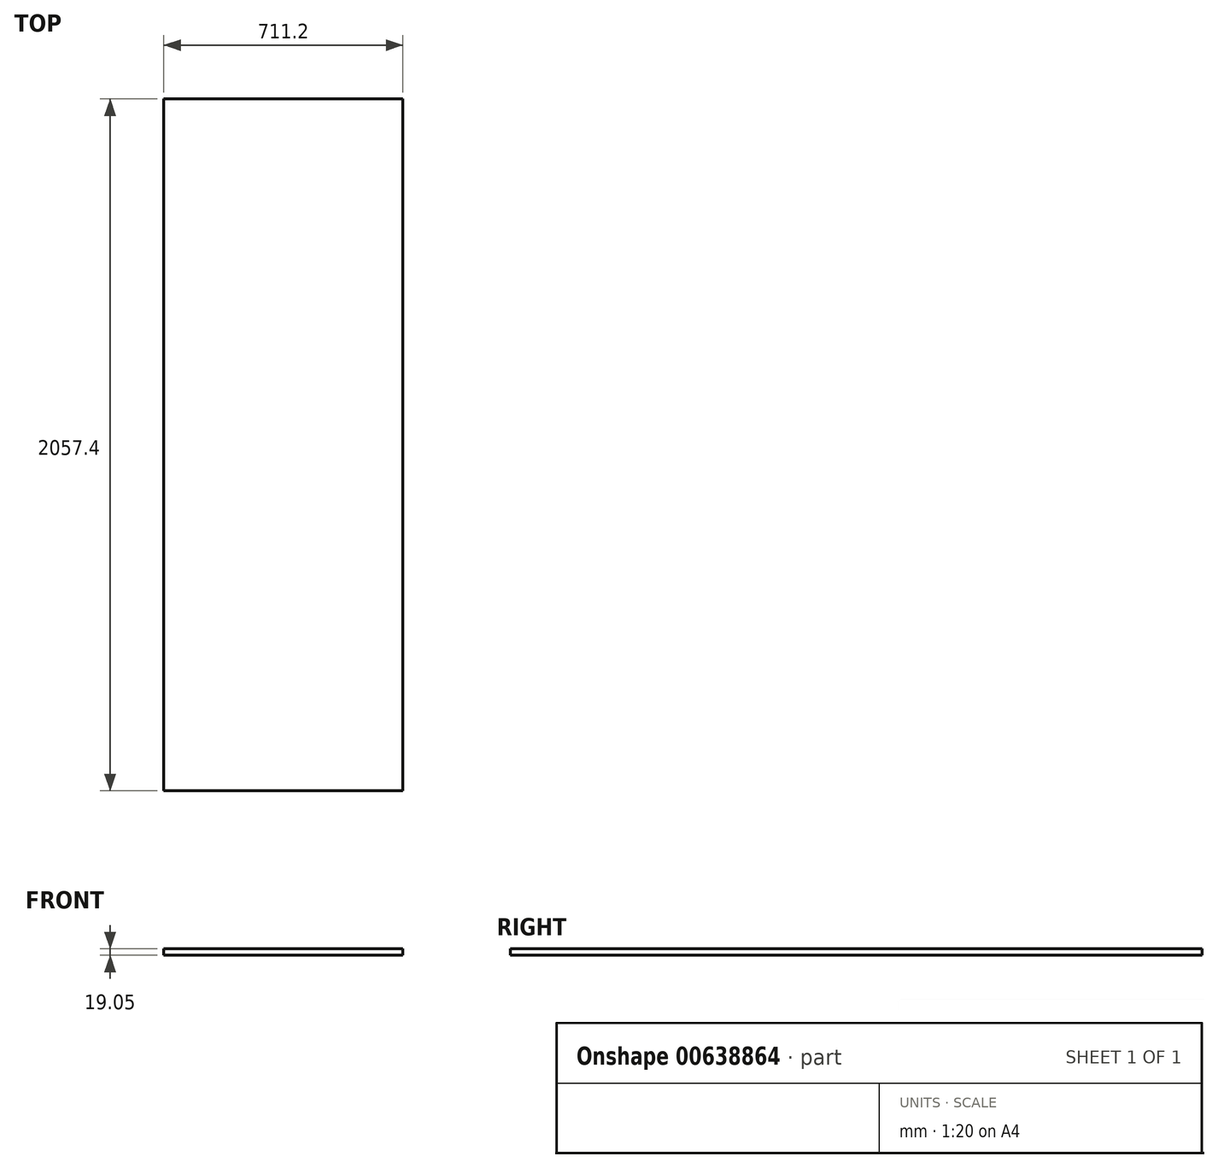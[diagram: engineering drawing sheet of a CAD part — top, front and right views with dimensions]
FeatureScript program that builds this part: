
annotation { "Feature Type Name" : "Feature", "Feature Type Description" : "" }
export const myFeature = defineFeature(function(context is Context, id is Id, definition is map)
    precondition{}
    {
        {
            var Q0;
            Q0=qCreatedBy(makeId("Top.planeOp"),FACE);
            var sketch = newSketch(context, id + "F0", { "sketchPlane" : qUnion([Q0])});
            skLineSegment(sketch, "E0.bottom", {"start": v(355.6, 1028.7) * mm, "end": v(-355.6, 1028.7) * mm});
            skLineSegment(sketch, "E0.top", {"start": v(355.6, -1028.7) * mm, "end": v(-355.6, -1028.7) * mm});
            skLineSegment(sketch, "E0.left", {"start": v(355.6, 1028.7) * mm, "end": v(355.6, -1028.7) * mm});
            skLineSegment(sketch, "E0.right", {"start": v(-355.6, 1028.7) * mm, "end": v(-355.6, -1028.7) * mm});
            skPoint(sketch, "E0.middle", {"position": v(0, 0) * mm});
            skSolve(sketch);
        }
        {
            var Q0;
            Q0=makeQuery(id+"F0.imprint","IMPRINT",FACE,{"disambiguationData":[TD([[makeQuery(id+"F0.imprint","IMPRINT",EDGE,{"derivedFrom":sQuery(id+"F0.wireOp",EDGE,"E0.bottom")}),1.0]])]});
            extrude(context, id + "F1", {"entities" : qUnion([Q0]), "depth" : 19.05 * mm, "offsetDistance" : 25.4 * mm});
        }
    });
